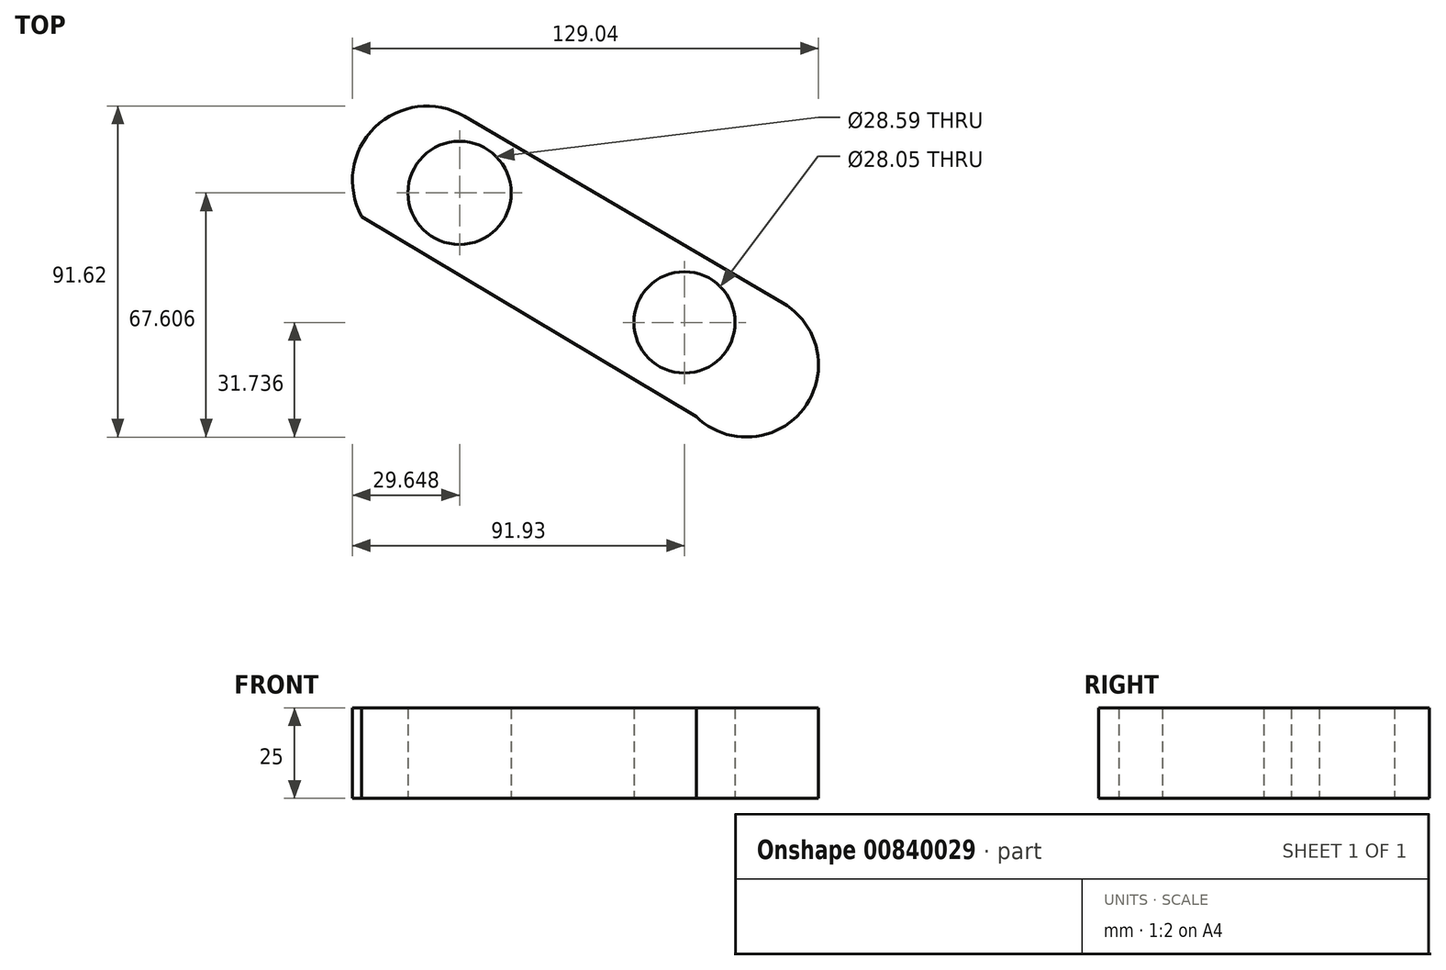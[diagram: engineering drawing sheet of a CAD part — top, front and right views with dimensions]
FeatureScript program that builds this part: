
annotation { "Feature Type Name" : "Feature", "Feature Type Description" : "" }
export const myFeature = defineFeature(function(context is Context, id is Id, definition is map)
    precondition{}
    {
        {
            var Q0;
            Q0=qCreatedBy(makeId("Top.planeOp"),FACE);
            var sketch = newSketch(context, id + "F0", { "sketchPlane" : qUnion([Q0])});
            skArc(sketch, "E0", {"start": v(-25.6, 49.9) * mm, "mid": v(-50.36, 46.85) * mm, "end": v(-53.97, 22.17) * mm});
            skLineSegment(sketch, "E1", {"start": v(-53.97, 22.17) * mm, "end": v(38.64, -33.26) * mm});
            skLineSegment(sketch, "E2", {"start": v(-25.6, 49.9) * mm, "end": v(62.62, -1.76) * mm});
            skArc(sketch, "E3", {"start": v(38.64, -33.26) * mm, "mid": v(68.41, -31.04) * mm, "end": v(62.62, -1.76) * mm});
            skCircle(sketch, "E4", {"center": v(-26.9, 28.7) * mm, "radius": 14.3 * mm});
            skCircle(sketch, "E5", {"center": v(35.38, -7.17) * mm, "radius": 14.03 * mm});
            skSolve(sketch);
        }
        {
            var Q0;
            Q0 = qSketchRegion(id + "F0", true);
            extrude(context, id + "F1", {"entities" : qUnion([Q0]), "depth" : 25 * mm, "offsetDistance" : 25 * mm});
        }
    });
